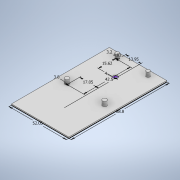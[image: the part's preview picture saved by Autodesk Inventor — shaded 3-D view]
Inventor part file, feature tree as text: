
AUTODESK INVENTOR PART (.ipt)
format: ipt  version: 2020 (Build 240168000, 168)  size: 129,024 bytes
history: native  units: mm
features: sketch x3, extrude x3
ambient origin geometry x8: Origin, YZ Plane, XZ Plane, XY Plane, X Axis, Y Axis, Z Axis, Center Point
bodies: Solid1 (feature_tree)
feature tree (6):
  sketch  "Sketch1"  dims[d0=52.05mm d1=88.8mm]
  sketch  "Sketch2"  dims[d2=3.8mm d4=17.05mm]
  extrude  "Extrusion1"  Depth=88.8mm
  sketch  "Sketch3"  dims[d5=3.2mm d6=13.95mm d7=42.5mm d8=5.0mm d9=0.0mm d10=1.0mm d11=0.0mm d12=4.83mm d13=4.0mm d15=5.0mm d16=0.0mm d17=15.62mm]
  extrude  "Extrusion2"  Depth=17.05mm
  extrude  "Extrusion3"  Depth=5.0mm
